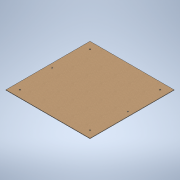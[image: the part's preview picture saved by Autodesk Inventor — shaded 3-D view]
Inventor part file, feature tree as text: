
AUTODESK INVENTOR PART (.ipt)
format: ipt  version: 2022 (Build 260153000, 153)  size: 128,000 bytes
history: native  units: mm
features: sketch x3, hole x2, other x1, extrude x1
ambient origin geometry x8: Origin, YZ Plane, XZ Plane, XY Plane, X Axis, Y Axis, Z Axis, Center Point
bodies: Body1 (feature_tree)
feature tree (7):
  other  "Sólido1"
  extrude  "Extrusão1"  Depth=4.0mm
  hole  "Furo1"  [1 undecoded]
  hole  "Furo2"  [1 undecoded]
  sketch  "Esboço1"  dims[d2=3.0mm d3=0.0mm]
  sketch  "Esboço2"  dims[d4=8.0mm d5=6.0mm d6=4.0mm d7=2.0mm d8=90.0deg d9=8.0mm d10=20.594885mm]
  sketch  "Esboço3"  dims[d11=8.0mm d12=6.0mm d13=4.0mm d14=2.0mm d15=90.0deg d16=8.0mm d17=20.594885mm d18=29.956mm d19=29.956mm]
note: 2 required parameter values undecoded (feature->parameter linkage not recoverable at this tier; creation-order binding heuristic only, values carry confidence <= 0.55)
